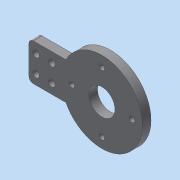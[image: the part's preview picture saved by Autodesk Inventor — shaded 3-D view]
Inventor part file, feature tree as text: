
AUTODESK INVENTOR PART (.ipt)
format: ipt  version: 2017 (Build 210142000, 142)  size: 137,728 bytes
history: native  units: in
note: dims shown in document units (in); Inventor stores cm internally (conversion verified against a paired STEP export)
features: other x8, extrude x2
ambient origin geometry x8: Origin, YZ Plane, XZ Plane, XY Plane, X Axis, Y Axis, Z Axis, Center Point
bodies: Solid1 (feature_tree)
feature tree (10):
  extrude  "plate"  Depth=2.3228in
  extrude  "motor hole"  Depth=0.125in
  other  "platethread1"
  other  "platethread2"
  other  "platethread3"
  other  "platethread4"
  other  "motorthread1"
  other  "motorthread2"
  other  "motorthread3"
  other  "motorthread4"
